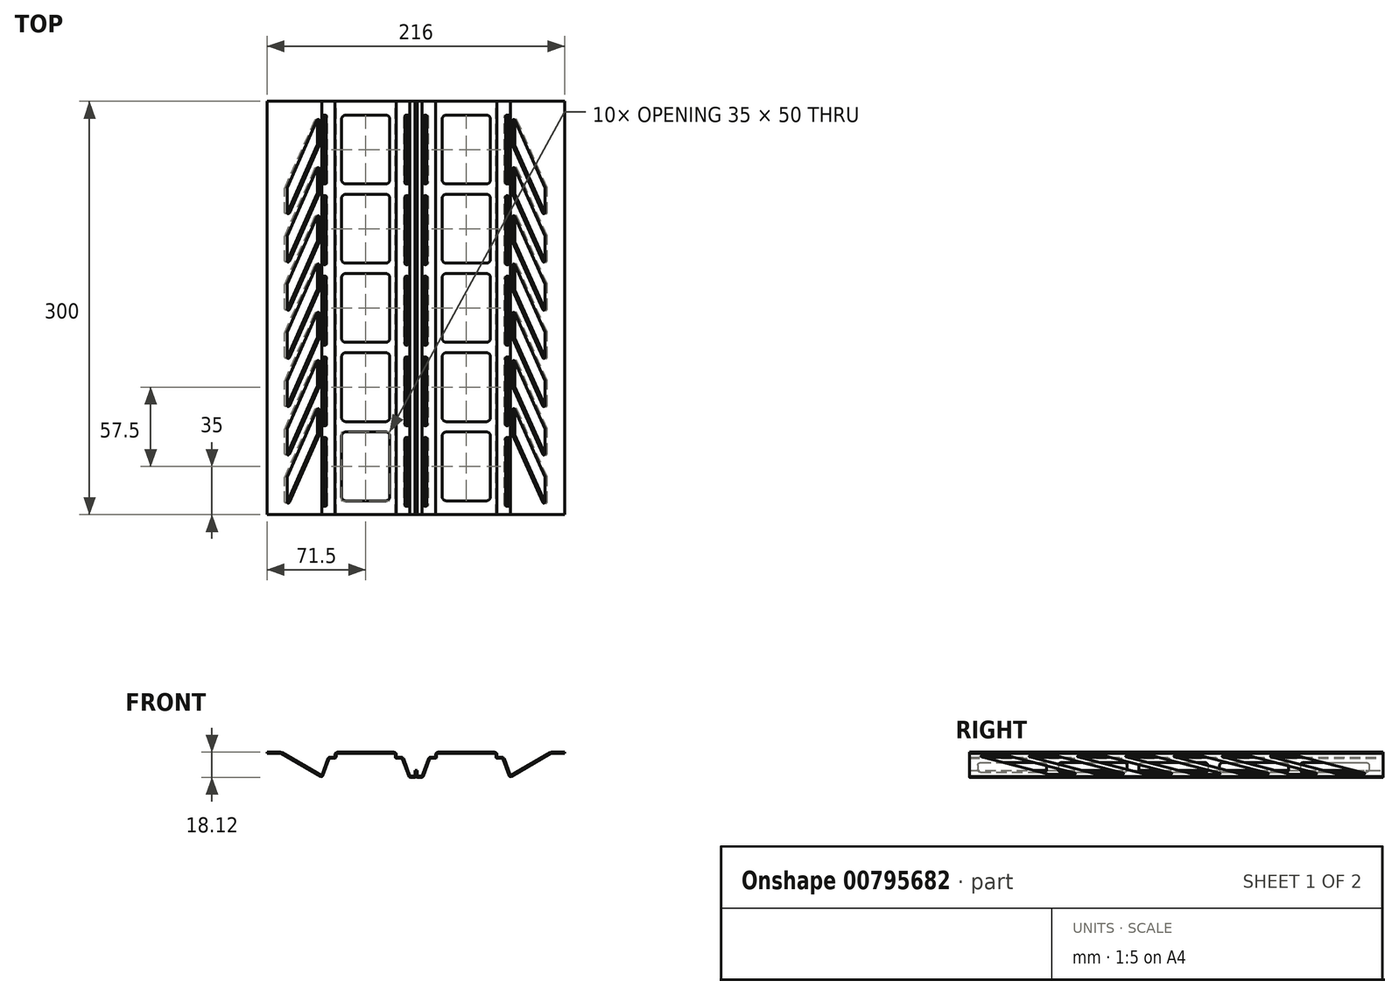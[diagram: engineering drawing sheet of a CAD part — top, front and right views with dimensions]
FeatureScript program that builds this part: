
annotation { "Feature Type Name" : "Feature", "Feature Type Description" : "" }
export const myFeature = defineFeature(function(context is Context, id is Id, definition is map)
    precondition{}
    {
        {
            var Q0;
            Q0=qCreatedBy(makeId("Front.planeOp"),FACE);
            var sketch = newSketch(context, id + "F0", { "sketchPlane" : qUnion([Q0])});
            skLineSegment(sketch, "E0", {"start": v(-0.8, 0) * mm, "end": v(-4.3, 0) * mm});
            skLineSegment(sketch, "E1", {"start": v(-5.24, 0.66) * mm, "end": v(-9.76, 13.08) * mm});
            skLineSegment(sketch, "E2", {"start": v(-10.7, 13.74) * mm, "end": v(-14, 13.74) * mm});
            skLineSegment(sketch, "E3", {"start": v(-63.24, 13.08) * mm, "end": v(-67.6, 1.12) * mm});
            skLineSegment(sketch, "E4", {"start": v(-69.03, 0.6) * mm, "end": v(-97.77, 17.19) * mm});
            skLineSegment(sketch, "E5", {"start": v(-98.27, 17.32) * mm, "end": v(-108, 17.32) * mm});
            skLineSegment(sketch, "E6", {"start": v(-57, 17.32) * mm, "end": v(-16, 17.32) * mm});
            skLineSegment(sketch, "E7", {"start": v(-58, 14.74) * mm, "end": v(-58, 16.32) * mm});
            skLineSegment(sketch, "E8", {"start": v(-36.5, 24.7) * mm, "end": v(-36.5, 3.7) * mm, "construction": true});
            skPoint(sketch, "E8.startSnap0", {"position": v(-36.5, 13.74) * mm});
            skLineSegment(sketch, "E9.MirrorCS", {"start": v(-15, 14.74) * mm, "end": v(-15, 16.32) * mm});
            skPoint(sketch, "E10.orphan", {"position": v(-63.46, 17.32) * mm});
            skLineSegment(sketch, "E11.trimOffspring", {"start": v(-59, 13.74) * mm, "end": v(-62.3, 13.74) * mm});
            skPoint(sketch, "E12.visualSharp", {"position": v(-15, 13.74) * mm});
            skArc(sketch, "E12.filletArc", {"start": v(-15, 14.74) * mm, "mid": v(-14.7, 14.03) * mm, "end": v(-14, 13.74) * mm});
            skPoint(sketch, "E13.visualSharp", {"position": v(-15, 17.32) * mm});
            skArc(sketch, "E13.filletArc", {"start": v(-15, 16.32) * mm, "mid": v(-15.3, 17.03) * mm, "end": v(-16, 17.32) * mm});
            skPoint(sketch, "E14.visualSharp", {"position": v(-58, 17.32) * mm});
            skArc(sketch, "E14.filletArc", {"start": v(-57, 17.32) * mm, "mid": v(-57.7, 17.03) * mm, "end": v(-58, 16.32) * mm});
            skPoint(sketch, "E15.visualSharp", {"position": v(-58, 13.74) * mm});
            skArc(sketch, "E15.filletArc", {"start": v(-59, 13.74) * mm, "mid": v(-58.3, 14.03) * mm, "end": v(-58, 14.74) * mm});
            skPoint(sketch, "E16.visualSharp", {"position": v(-63, 13.74) * mm});
            skArc(sketch, "E16.filletArc", {"start": v(-62.3, 13.74) * mm, "mid": v(-62.87, 13.56) * mm, "end": v(-63.24, 13.08) * mm});
            skPoint(sketch, "E17.visualSharp", {"position": v(-10, 13.74) * mm});
            skArc(sketch, "E17.filletArc", {"start": v(-9.76, 13.08) * mm, "mid": v(-10.13, 13.56) * mm, "end": v(-10.7, 13.74) * mm});
            skPoint(sketch, "E18.visualSharp", {"position": v(-5, 0) * mm});
            skArc(sketch, "E18.filletArc", {"start": v(-5.24, 0.66) * mm, "mid": v(-4.87, 0.18) * mm, "end": v(-4.3, 0) * mm});
            skPoint(sketch, "E19.visualSharp", {"position": v(-68, 0) * mm});
            skArc(sketch, "E19.filletArc", {"start": v(-69.03, 0.6) * mm, "mid": v(-68.2, 0.52) * mm, "end": v(-67.6, 1.12) * mm});
            skPoint(sketch, "E20.visualSharp", {"position": v(-98, 17.32) * mm});
            skArc(sketch, "E20.filletArc", {"start": v(-97.77, 17.19) * mm, "mid": v(-98, 17.29) * mm, "end": v(-98.27, 17.32) * mm});
            skLineSegment(sketch, "E21.0", {"start": v(-68.43, 1.17) * mm, "end": v(-97.37, 17.88) * mm});
            skLineSegment(sketch, "E21.1", {"start": v(-64, 13.35) * mm, "end": v(-68.43, 1.17) * mm});
            skArc(sketch, "E21.2", {"start": v(-62.3, 14.54) * mm, "mid": v(-63.33, 14.21) * mm, "end": v(-64, 13.35) * mm});
            skLineSegment(sketch, "E21.3", {"start": v(-10.7, 14.54) * mm, "end": v(-14.2, 14.54) * mm});
            skArc(sketch, "E21.4", {"start": v(-9, 13.35) * mm, "mid": v(-9.67, 14.21) * mm, "end": v(-10.7, 14.54) * mm});
            skLineSegment(sketch, "E21.5", {"start": v(-4.44, 0.8) * mm, "end": v(-9, 13.35) * mm});
            skLineSegment(sketch, "E21.6", {"start": v(-0.8, 0.8) * mm, "end": v(-4.44, 0.8) * mm});
            skLineSegment(sketch, "E21.7", {"start": v(-14.2, 14.54) * mm, "end": v(-14.2, 16.32) * mm});
            skArc(sketch, "E21.8", {"start": v(-14.2, 16.32) * mm, "mid": v(-14.73, 17.6) * mm, "end": v(-16, 18.12) * mm});
            skLineSegment(sketch, "E21.9", {"start": v(-57, 18.12) * mm, "end": v(-16, 18.12) * mm});
            skArc(sketch, "E21.10", {"start": v(-57, 18.12) * mm, "mid": v(-58.27, 17.6) * mm, "end": v(-58.8, 16.32) * mm});
            skLineSegment(sketch, "E21.11", {"start": v(-58.8, 14.54) * mm, "end": v(-58.8, 16.32) * mm});
            skLineSegment(sketch, "E21.12", {"start": v(-58.8, 14.54) * mm, "end": v(-62.3, 14.54) * mm});
            skLineSegment(sketch, "E22.0", {"start": v(-98.27, 18.12) * mm, "end": v(-108, 18.12) * mm});
            skArc(sketch, "E22.1", {"start": v(-97.37, 17.88) * mm, "mid": v(-97.8, 18.06) * mm, "end": v(-98.27, 18.12) * mm});
            skLineSegment(sketch, "E23", {"start": v(-108, 18.12) * mm, "end": v(-108, 17.32) * mm});
            skLineSegment(sketch, "E24.0", {"start": v(-0.8, 0.8) * mm, "end": v(-0.8, 4.9) * mm});
            skLineSegment(sketch, "E25", {"start": v(0, 4.9) * mm, "end": v(-0.8, 4.9) * mm});
            skLineSegment(sketch, "E26", {"start": v(0, 4.9) * mm, "end": v(0, 0.8) * mm});
            skPoint(sketch, "E27.visualSharp", {"position": v(0, 0) * mm});
            skArc(sketch, "E27.filletArc", {"start": v(-0.8, 0) * mm, "mid": v(-0.23, 0.23) * mm, "end": v(0, 0.8) * mm});
            skSolve(sketch);
        }
        {
            var Q0;
            Q0=makeQuery(id+"F0.imprint","IMPRINT",FACE,{"disambiguationData":[TD([[makeQuery(id+"F0.imprint","IMPRINT",EDGE,{"derivedFrom":sQuery(id+"F0.wireOp",EDGE,"E0")}),-1.0]])]});
            extrude(context, id + "F1", {"entities" : qUnion([Q0]), "depth" : 300 * mm, "offsetDistance" : 25 * mm});
        }
        {
            var Q0;
            Q0=makeQuery(id+"F1.opExtrude","SWEPT_FACE",FACE,{"disambiguationData":[OSD([sQuery(id+"F0.wireOp",EDGE,"E21.9")])]});
            var sketch = newSketch(context, id + "F2", { "sketchPlane" : qUnion([Q0])});
            skLineSegment(sketch, "E28", {"start": v(-36.5, 0) * mm, "end": v(-36.5, -305.2) * mm, "construction": true});
            skPoint(sketch, "E29", {"position": v(-36.5, -35) * mm});
            skLineSegment(sketch, "E30.bottom", {"start": v(-22, -60) * mm, "end": v(-51, -60) * mm});
            skLineSegment(sketch, "E30.top", {"start": v(-22, -10) * mm, "end": v(-51, -10) * mm});
            skLineSegment(sketch, "E30.left", {"start": v(-19, -57) * mm, "end": v(-19, -13) * mm});
            skLineSegment(sketch, "E30.right", {"start": v(-54, -57) * mm, "end": v(-54, -13) * mm});
            skPoint(sketch, "E31.visualSharp", {"position": v(-54, -10) * mm});
            skArc(sketch, "E31.filletArc", {"start": v(-51, -10) * mm, "mid": v(-53.12, -10.88) * mm, "end": v(-54, -13) * mm});
            skPoint(sketch, "E32.visualSharp", {"position": v(-19, -10) * mm});
            skArc(sketch, "E32.filletArc", {"start": v(-19, -13) * mm, "mid": v(-19.88, -10.88) * mm, "end": v(-22, -10) * mm});
            skPoint(sketch, "E33.visualSharp", {"position": v(-19, -60) * mm});
            skArc(sketch, "E33.filletArc", {"start": v(-22, -60) * mm, "mid": v(-19.88, -59.12) * mm, "end": v(-19, -57) * mm});
            skPoint(sketch, "E34.visualSharp", {"position": v(-54, -60) * mm});
            skArc(sketch, "E34.filletArc", {"start": v(-54, -57) * mm, "mid": v(-53.12, -59.12) * mm, "end": v(-51, -60) * mm});
            skLineSegment(sketch, "E35.0.1.0", {"start": v(-22, -67.5) * mm, "end": v(-51, -67.5) * mm});
            skArc(sketch, "E35.0.1.1", {"start": v(-51, -67.5) * mm, "mid": v(-53.12, -68.38) * mm, "end": v(-54, -70.5) * mm});
            skLineSegment(sketch, "E35.0.1.2", {"start": v(-54, -114.5) * mm, "end": v(-54, -70.5) * mm});
            skArc(sketch, "E35.0.1.3", {"start": v(-54, -114.5) * mm, "mid": v(-53.12, -116.62) * mm, "end": v(-51, -117.5) * mm});
            skLineSegment(sketch, "E35.0.1.4", {"start": v(-22, -117.5) * mm, "end": v(-51, -117.5) * mm});
            skArc(sketch, "E35.0.1.5", {"start": v(-22, -117.5) * mm, "mid": v(-19.88, -116.62) * mm, "end": v(-19, -114.5) * mm});
            skLineSegment(sketch, "E35.0.1.6", {"start": v(-19, -114.5) * mm, "end": v(-19, -70.5) * mm});
            skArc(sketch, "E35.0.1.7", {"start": v(-19, -70.5) * mm, "mid": v(-19.88, -68.38) * mm, "end": v(-22, -67.5) * mm});
            skLineSegment(sketch, "E35.0.2.0", {"start": v(-22, -125) * mm, "end": v(-51, -125) * mm});
            skArc(sketch, "E35.0.2.1", {"start": v(-51, -125) * mm, "mid": v(-53.12, -125.88) * mm, "end": v(-54, -128) * mm});
            skLineSegment(sketch, "E35.0.2.2", {"start": v(-54, -172) * mm, "end": v(-54, -128) * mm});
            skArc(sketch, "E35.0.2.3", {"start": v(-54, -172) * mm, "mid": v(-53.12, -174.12) * mm, "end": v(-51, -175) * mm});
            skLineSegment(sketch, "E35.0.2.4", {"start": v(-22, -175) * mm, "end": v(-51, -175) * mm});
            skArc(sketch, "E35.0.2.5", {"start": v(-22, -175) * mm, "mid": v(-19.88, -174.12) * mm, "end": v(-19, -172) * mm});
            skLineSegment(sketch, "E35.0.2.6", {"start": v(-19, -172) * mm, "end": v(-19, -128) * mm});
            skArc(sketch, "E35.0.2.7", {"start": v(-19, -128) * mm, "mid": v(-19.88, -125.88) * mm, "end": v(-22, -125) * mm});
            skLineSegment(sketch, "E35.0.3.0", {"start": v(-22, -182.5) * mm, "end": v(-51, -182.5) * mm});
            skArc(sketch, "E35.0.3.1", {"start": v(-51, -182.5) * mm, "mid": v(-53.12, -183.38) * mm, "end": v(-54, -185.5) * mm});
            skLineSegment(sketch, "E35.0.3.2", {"start": v(-54, -229.5) * mm, "end": v(-54, -185.5) * mm});
            skArc(sketch, "E35.0.3.3", {"start": v(-54, -229.5) * mm, "mid": v(-53.12, -231.62) * mm, "end": v(-51, -232.5) * mm});
            skLineSegment(sketch, "E35.0.3.4", {"start": v(-22, -232.5) * mm, "end": v(-51, -232.5) * mm});
            skArc(sketch, "E35.0.3.5", {"start": v(-22, -232.5) * mm, "mid": v(-19.88, -231.62) * mm, "end": v(-19, -229.5) * mm});
            skLineSegment(sketch, "E35.0.3.6", {"start": v(-19, -229.5) * mm, "end": v(-19, -185.5) * mm});
            skArc(sketch, "E35.0.3.7", {"start": v(-19, -185.5) * mm, "mid": v(-19.88, -183.38) * mm, "end": v(-22, -182.5) * mm});
            skLineSegment(sketch, "E35.0.4.0", {"start": v(-22, -240) * mm, "end": v(-51, -240) * mm});
            skArc(sketch, "E35.0.4.1", {"start": v(-51, -240) * mm, "mid": v(-53.12, -240.88) * mm, "end": v(-54, -243) * mm});
            skLineSegment(sketch, "E35.0.4.2", {"start": v(-54, -287) * mm, "end": v(-54, -243) * mm});
            skArc(sketch, "E35.0.4.3", {"start": v(-54, -287) * mm, "mid": v(-53.12, -289.12) * mm, "end": v(-51, -290) * mm});
            skLineSegment(sketch, "E35.0.4.4", {"start": v(-22, -290) * mm, "end": v(-51, -290) * mm});
            skArc(sketch, "E35.0.4.5", {"start": v(-22, -290) * mm, "mid": v(-19.88, -289.12) * mm, "end": v(-19, -287) * mm});
            skLineSegment(sketch, "E35.0.4.6", {"start": v(-19, -287) * mm, "end": v(-19, -243) * mm});
            skArc(sketch, "E35.0.4.7", {"start": v(-19, -243) * mm, "mid": v(-19.88, -240.88) * mm, "end": v(-22, -240) * mm});
            skLineSegment(sketch, "E35.direction1", {"start": v(-51, -10) * mm, "end": v(-26, -10) * mm, "construction": true});
            skLineSegment(sketch, "E35.direction2", {"start": v(-51, -10) * mm, "end": v(-51, -67.5) * mm, "construction": true});
            skSolve(sketch);
        }
        {
            var Q0;
            Q0 = qSketchRegion(id + "F2", true);
            extrude(context, id + "F3", {"entities" : qUnion([Q0]), "operationType" : NewBodyOperationType.REMOVE, "oppositeDirection" : true, "depth" : 25 * mm, "offsetDistance" : 25 * mm});
        }
        {
            var Q0;
            Q0=makeQuery(id+"F1.opExtrude","SWEPT_FACE",FACE,{"disambiguationData":[OSD([sQuery(id+"F0.wireOp",EDGE,"E21.5")])]});
            var sketch = newSketch(context, id + "F4", { "sketchPlane" : qUnion([Q0])});
            skLineSegment(sketch, "E36", {"start": v(0, 8.95) * mm, "end": v(-300, 8.95) * mm, "construction": true});
            skPoint(sketch, "E37", {"position": v(-10, 8.95) * mm});
            skLineSegment(sketch, "E38.bottom", {"start": v(-12, 5.27) * mm, "end": v(-58, 5.27) * mm});
            skLineSegment(sketch, "E38.top", {"start": v(-12, 12.63) * mm, "end": v(-58, 12.63) * mm});
            skLineSegment(sketch, "E38.left", {"start": v(-10, 7.27) * mm, "end": v(-10, 10.63) * mm});
            skLineSegment(sketch, "E38.right", {"start": v(-60, 7.27) * mm, "end": v(-60, 10.63) * mm});
            skPoint(sketch, "E39.visualSharp", {"position": v(-10, 5.27) * mm});
            skArc(sketch, "E39.filletArc", {"start": v(-12, 5.27) * mm, "mid": v(-10.59, 5.86) * mm, "end": v(-10, 7.27) * mm});
            skPoint(sketch, "E40.visualSharp", {"position": v(-10, 12.63) * mm});
            skArc(sketch, "E40.filletArc", {"start": v(-10, 10.63) * mm, "mid": v(-10.59, 12.04) * mm, "end": v(-12, 12.63) * mm});
            skPoint(sketch, "E41.visualSharp", {"position": v(-60, 5.27) * mm});
            skArc(sketch, "E41.filletArc", {"start": v(-60, 7.27) * mm, "mid": v(-59.41, 5.86) * mm, "end": v(-58, 5.27) * mm});
            skPoint(sketch, "E42.visualSharp", {"position": v(-60, 12.63) * mm});
            skArc(sketch, "E42.filletArc", {"start": v(-58, 12.63) * mm, "mid": v(-59.41, 12.04) * mm, "end": v(-60, 10.63) * mm});
            skLineSegment(sketch, "E43.1.0.0", {"start": v(-67.5, 7.27) * mm, "end": v(-67.5, 10.63) * mm});
            skArc(sketch, "E43.1.0.1", {"start": v(-69.5, 5.27) * mm, "mid": v(-68.09, 5.86) * mm, "end": v(-67.5, 7.27) * mm});
            skArc(sketch, "E43.1.0.2", {"start": v(-67.5, 10.63) * mm, "mid": v(-68.09, 12.04) * mm, "end": v(-69.5, 12.63) * mm});
            skLineSegment(sketch, "E43.1.0.3", {"start": v(-69.5, 12.63) * mm, "end": v(-115.5, 12.63) * mm});
            skLineSegment(sketch, "E43.1.0.4", {"start": v(-69.5, 5.27) * mm, "end": v(-115.5, 5.27) * mm});
            skArc(sketch, "E43.1.0.5", {"start": v(-117.5, 7.27) * mm, "mid": v(-116.91, 5.86) * mm, "end": v(-115.5, 5.27) * mm});
            skLineSegment(sketch, "E43.1.0.6", {"start": v(-117.5, 7.27) * mm, "end": v(-117.5, 10.63) * mm});
            skArc(sketch, "E43.1.0.7", {"start": v(-115.5, 12.63) * mm, "mid": v(-116.91, 12.04) * mm, "end": v(-117.5, 10.63) * mm});
            skLineSegment(sketch, "E43.2.0.0", {"start": v(-125, 7.27) * mm, "end": v(-125, 10.63) * mm});
            skArc(sketch, "E43.2.0.1", {"start": v(-127, 5.27) * mm, "mid": v(-125.59, 5.86) * mm, "end": v(-125, 7.27) * mm});
            skArc(sketch, "E43.2.0.2", {"start": v(-125, 10.63) * mm, "mid": v(-125.59, 12.04) * mm, "end": v(-127, 12.63) * mm});
            skLineSegment(sketch, "E43.2.0.3", {"start": v(-127, 12.63) * mm, "end": v(-173, 12.63) * mm});
            skLineSegment(sketch, "E43.2.0.4", {"start": v(-127, 5.27) * mm, "end": v(-173, 5.27) * mm});
            skArc(sketch, "E43.2.0.5", {"start": v(-175, 7.27) * mm, "mid": v(-174.41, 5.86) * mm, "end": v(-173, 5.27) * mm});
            skLineSegment(sketch, "E43.2.0.6", {"start": v(-175, 7.27) * mm, "end": v(-175, 10.63) * mm});
            skArc(sketch, "E43.2.0.7", {"start": v(-173, 12.63) * mm, "mid": v(-174.41, 12.04) * mm, "end": v(-175, 10.63) * mm});
            skLineSegment(sketch, "E43.3.0.0", {"start": v(-182.5, 7.27) * mm, "end": v(-182.5, 10.63) * mm});
            skArc(sketch, "E43.3.0.1", {"start": v(-184.5, 5.27) * mm, "mid": v(-183.09, 5.86) * mm, "end": v(-182.5, 7.27) * mm});
            skArc(sketch, "E43.3.0.2", {"start": v(-182.5, 10.63) * mm, "mid": v(-183.09, 12.04) * mm, "end": v(-184.5, 12.63) * mm});
            skLineSegment(sketch, "E43.3.0.3", {"start": v(-184.5, 12.63) * mm, "end": v(-230.5, 12.63) * mm});
            skLineSegment(sketch, "E43.3.0.4", {"start": v(-184.5, 5.27) * mm, "end": v(-230.5, 5.27) * mm});
            skArc(sketch, "E43.3.0.5", {"start": v(-232.5, 7.27) * mm, "mid": v(-231.91, 5.86) * mm, "end": v(-230.5, 5.27) * mm});
            skLineSegment(sketch, "E43.3.0.6", {"start": v(-232.5, 7.27) * mm, "end": v(-232.5, 10.63) * mm});
            skArc(sketch, "E43.3.0.7", {"start": v(-230.5, 12.63) * mm, "mid": v(-231.91, 12.04) * mm, "end": v(-232.5, 10.63) * mm});
            skLineSegment(sketch, "E43.4.0.0", {"start": v(-240, 7.27) * mm, "end": v(-240, 10.63) * mm});
            skArc(sketch, "E43.4.0.1", {"start": v(-242, 5.27) * mm, "mid": v(-240.59, 5.86) * mm, "end": v(-240, 7.27) * mm});
            skArc(sketch, "E43.4.0.2", {"start": v(-240, 10.63) * mm, "mid": v(-240.59, 12.04) * mm, "end": v(-242, 12.63) * mm});
            skLineSegment(sketch, "E43.4.0.3", {"start": v(-242, 12.63) * mm, "end": v(-288, 12.63) * mm});
            skLineSegment(sketch, "E43.4.0.4", {"start": v(-242, 5.27) * mm, "end": v(-288, 5.27) * mm});
            skArc(sketch, "E43.4.0.5", {"start": v(-290, 7.27) * mm, "mid": v(-289.41, 5.86) * mm, "end": v(-288, 5.27) * mm});
            skLineSegment(sketch, "E43.4.0.6", {"start": v(-290, 7.27) * mm, "end": v(-290, 10.63) * mm});
            skArc(sketch, "E43.4.0.7", {"start": v(-288, 12.63) * mm, "mid": v(-289.41, 12.04) * mm, "end": v(-290, 10.63) * mm});
            skLineSegment(sketch, "E43.direction1", {"start": v(-10, 7.27) * mm, "end": v(-67.5, 7.27) * mm, "construction": true});
            skSolve(sketch);
        }
        {
            var Q0;
            Q0=qCreatedBy(makeId("Right.planeOp"),FACE);
            cPlane(context, id + "F5", {"entities" : qUnion([Q0]), "cplaneType" : CPlaneType.OFFSET, "offset" : 36.5 * mm, "oppositeDirection" : true, "width" : 150 * mm, "height" : 150 * mm});
        }
        {
            var Q0;
            Q0=qCreatedBy(id+"F5.planeOp",FACE);
            var sketch = newSketch(context, id + "F6", { "sketchPlane" : qUnion([Q0])});
            skLineSegment(sketch, "E44.0", {"start": v(-60, 5.5) * mm, "end": v(-60, 8.65) * mm});
            skEllipticalArc(sketch, "E45.0", {});
            skLineSegment(sketch, "E46.0", {"start": v(-12, 3.62) * mm, "end": v(-58, 3.62) * mm});
            skLineSegment(sketch, "E47.0", {"start": v(-12, 10.53) * mm, "end": v(-58, 10.53) * mm});
            skPoint(sketch, "E48.0", {"position": v(-59.41, 9.98) * mm});
            skEllipticalArc(sketch, "E49.0", {});
            skEllipticalArc(sketch, "E50.0", {});
            skLineSegment(sketch, "E51.0", {"start": v(-10, 5.5) * mm, "end": v(-10, 8.65) * mm});
            skEllipticalArc(sketch, "E52.0", {});
            skPoint(sketch, "E53.0.end.orphan", {"position": v(-115.5, 3.62) * mm});
            skPoint(sketch, "E53.0.start.orphan", {"position": v(-69.5, 3.62) * mm});
            skPoint(sketch, "E54.0.end.orphan", {"position": v(-67.5, 5.5) * mm});
            skPoint(sketch, "E55.0.end.orphan", {"position": v(-67.5, 8.65) * mm});
            skLineSegment(sketch, "E56.1.0.0", {"start": v(-70.5, 3.62) * mm, "end": v(-116.5, 3.62) * mm});
            skEllipticalArc(sketch, "E56.1.0.1", {});
            skLineSegment(sketch, "E56.1.0.2", {"start": v(-118.5, 5.5) * mm, "end": v(-118.5, 8.65) * mm});
            skEllipticalArc(sketch, "E56.1.0.3", {});
            skLineSegment(sketch, "E56.1.0.4", {"start": v(-70.5, 10.53) * mm, "end": v(-116.5, 10.53) * mm});
            skEllipticalArc(sketch, "E56.1.0.5", {});
            skLineSegment(sketch, "E56.1.0.6", {"start": v(-68.5, 5.5) * mm, "end": v(-68.5, 8.65) * mm});
            skEllipticalArc(sketch, "E56.1.0.7", {});
            skLineSegment(sketch, "E56.2.0.0", {"start": v(-129, 3.62) * mm, "end": v(-175, 3.62) * mm});
            skEllipticalArc(sketch, "E56.2.0.1", {});
            skLineSegment(sketch, "E56.2.0.2", {"start": v(-177, 5.5) * mm, "end": v(-177, 8.65) * mm});
            skEllipticalArc(sketch, "E56.2.0.3", {});
            skLineSegment(sketch, "E56.2.0.4", {"start": v(-129, 10.53) * mm, "end": v(-175, 10.53) * mm});
            skEllipticalArc(sketch, "E56.2.0.5", {});
            skLineSegment(sketch, "E56.2.0.6", {"start": v(-127, 5.5) * mm, "end": v(-127, 8.65) * mm});
            skEllipticalArc(sketch, "E56.2.0.7", {});
            skLineSegment(sketch, "E56.3.0.0", {"start": v(-187.5, 3.62) * mm, "end": v(-233.5, 3.62) * mm});
            skEllipticalArc(sketch, "E56.3.0.1", {});
            skLineSegment(sketch, "E56.3.0.2", {"start": v(-235.5, 5.5) * mm, "end": v(-235.5, 8.65) * mm});
            skEllipticalArc(sketch, "E56.3.0.3", {});
            skLineSegment(sketch, "E56.3.0.4", {"start": v(-187.5, 10.53) * mm, "end": v(-233.5, 10.53) * mm});
            skEllipticalArc(sketch, "E56.3.0.5", {});
            skLineSegment(sketch, "E56.3.0.6", {"start": v(-185.5, 5.5) * mm, "end": v(-185.5, 8.65) * mm});
            skEllipticalArc(sketch, "E56.3.0.7", {});
            skLineSegment(sketch, "E56.4.0.0", {"start": v(-246, 3.62) * mm, "end": v(-292, 3.62) * mm});
            skEllipticalArc(sketch, "E56.4.0.1", {});
            skLineSegment(sketch, "E56.4.0.2", {"start": v(-294, 5.5) * mm, "end": v(-294, 8.65) * mm});
            skEllipticalArc(sketch, "E56.4.0.3", {});
            skLineSegment(sketch, "E56.4.0.4", {"start": v(-246, 10.53) * mm, "end": v(-292, 10.53) * mm});
            skEllipticalArc(sketch, "E56.4.0.5", {});
            skLineSegment(sketch, "E56.4.0.6", {"start": v(-244, 5.5) * mm, "end": v(-244, 8.65) * mm});
            skEllipticalArc(sketch, "E56.4.0.7", {});
            skLineSegment(sketch, "E56.direction1", {"start": v(-58, 3.62) * mm, "end": v(-116.5, 3.62) * mm, "construction": true});
            const initialGuessF6  = {"E45.0": [-0.058, 0.005498463103929539, 1, 0, 0.002, 0.001879385241571812, 3.141592653589793, 4.71238898038469], "E49.0": [-0.058, 0.008654560251329744, 1, 0, 0.002, 0.001879385241571817, 1.5707963267948966, 3.141592653589793], "E50.0": [-0.012, 0.005498463103929544, 1, 0, 0.002, 0.001879385241571817, 4.71238898038469, 0], "E52.0": [-0.012, 0.00865456025132975, 1, 0, 0.002, 0.001879385241571817, 0, 1.5707963267948966], "E56.1.0.1": [-0.1165, 0.005498463103929539, 1, 0, 0.002, 0.001879385241571812, 3.141592653589793, 4.71238898038469], "E56.1.0.3": [-0.1165, 0.008654560251329744, 1, 0, 0.002, 0.001879385241571817, 1.5707963267948966, 3.141592653589793], "E56.1.0.5": [-0.0705, 0.00865456025132975, 1, 0, 0.002, 0.001879385241571817, 0, 1.5707963267948966], "E56.1.0.7": [-0.0705, 0.005498463103929544, 1, 0, 0.002, 0.001879385241571817, 4.71238898038469, 0], "E56.2.0.1": [-0.175, 0.005498463103929539, 1, 0, 0.002, 0.001879385241571812, 3.141592653589793, 4.71238898038469], "E56.2.0.3": [-0.175, 0.008654560251329744, 1, 0, 0.002, 0.001879385241571817, 1.5707963267948966, 3.141592653589793], "E56.2.0.5": [-0.129, 0.00865456025132975, 1, 0, 0.002, 0.001879385241571817, 0, 1.5707963267948966], "E56.2.0.7": [-0.129, 0.005498463103929544, 1, 0, 0.002, 0.001879385241571817, 4.71238898038469, 0], "E56.3.0.1": [-0.2335, 0.005498463103929539, 1, 0, 0.002, 0.001879385241571812, 3.141592653589793, 4.71238898038469], "E56.3.0.3": [-0.2335, 0.008654560251329744, 1, 0, 0.002, 0.001879385241571817, 1.5707963267948966, 3.141592653589793], "E56.3.0.5": [-0.1875, 0.00865456025132975, 1, 0, 0.002, 0.001879385241571817, 0, 1.5707963267948966], "E56.3.0.7": [-0.1875, 0.005498463103929544, 1, 0, 0.002, 0.001879385241571817, 4.71238898038469, 0], "E56.4.0.1": [-0.292, 0.005498463103929539, 1, 0, 0.002, 0.001879385241571812, 3.141592653589793, 4.71238898038469], "E56.4.0.3": [-0.292, 0.008654560251329744, 1, 0, 0.002, 0.001879385241571817, 1.5707963267948966, 3.141592653589793], "E56.4.0.5": [-0.246, 0.00865456025132975, 1, 0, 0.002, 0.001879385241571817, 0, 1.5707963267948966], "E56.4.0.7": [-0.246, 0.005498463103929544, 1, 0, 0.002, 0.001879385241571817, 4.71238898038469, 0]};
            skSetInitialGuess(sketch, initialGuessF6);
            skSolve(sketch);
        }
        {
            var Q0;
            Q0 = qSketchRegion(id + "F6", true);
            extrude(context, id + "F7", {"entities" : qUnion([Q0]), "operationType" : NewBodyOperationType.REMOVE, "endBound" : BoundingType.SYMMETRIC, "depth" : 70 * mm, "offsetDistance" : 25 * mm});
        }
        {
            var Q0;
            Q0=makeQuery(id+"F1.opExtrude","SWEPT_BODY",BODY,{"disambiguationData":[OSD([sQuery(id+"F0.wireOp",EDGE,"E0"),sQuery(id+"F0.wireOp",EDGE,"E1"),sQuery(id+"F0.wireOp",EDGE,"E2"),sQuery(id+"F0.wireOp",EDGE,"E3"),sQuery(id+"F0.wireOp",EDGE,"E4"),sQuery(id+"F0.wireOp",EDGE,"E5"),sQuery(id+"F0.wireOp",EDGE,"E6"),sQuery(id+"F0.wireOp",EDGE,"E7"),sQuery(id+"F0.wireOp",EDGE,"E9.MirrorCS"),sQuery(id+"F0.wireOp",EDGE,"E11.trimOffspring"),sQuery(id+"F0.wireOp",EDGE,"E12.filletArc"),sQuery(id+"F0.wireOp",EDGE,"E13.filletArc"),sQuery(id+"F0.wireOp",EDGE,"E14.filletArc"),sQuery(id+"F0.wireOp",EDGE,"E15.filletArc"),sQuery(id+"F0.wireOp",EDGE,"E16.filletArc"),sQuery(id+"F0.wireOp",EDGE,"E17.filletArc"),sQuery(id+"F0.wireOp",EDGE,"E18.filletArc"),sQuery(id+"F0.wireOp",EDGE,"E19.filletArc"),sQuery(id+"F0.wireOp",EDGE,"E20.filletArc"),sQuery(id+"F0.wireOp",EDGE,"E21.0"),sQuery(id+"F0.wireOp",EDGE,"E21.1"),sQuery(id+"F0.wireOp",EDGE,"E21.2"),sQuery(id+"F0.wireOp",EDGE,"E21.3"),sQuery(id+"F0.wireOp",EDGE,"E21.4"),sQuery(id+"F0.wireOp",EDGE,"E21.5"),sQuery(id+"F0.wireOp",EDGE,"E21.6"),sQuery(id+"F0.wireOp",EDGE,"E21.7"),sQuery(id+"F0.wireOp",EDGE,"E21.8"),sQuery(id+"F0.wireOp",EDGE,"E21.9"),sQuery(id+"F0.wireOp",EDGE,"E21.10"),sQuery(id+"F0.wireOp",EDGE,"E21.11"),sQuery(id+"F0.wireOp",EDGE,"E21.12"),sQuery(id+"F0.wireOp",EDGE,"E22.0"),sQuery(id+"F0.wireOp",EDGE,"E22.1"),sQuery(id+"F0.wireOp",EDGE,"E23"),sQuery(id+"F0.wireOp",EDGE,"E24.0"),sQuery(id+"F0.wireOp",EDGE,"E25"),sQuery(id+"F0.wireOp",EDGE,"E26"),sQuery(id+"F0.wireOp",EDGE,"E27.filletArc")])]});
            var Q1;
            Q1=qCreatedBy(makeId("Right.planeOp"),FACE);
            mirror(context, id + "F8", {"operationType" : NewBodyOperationType.ADD, "entities" : qUnion([Q0]), "mirrorPlane" : qUnion([Q1])});
        }
        {
            var Q0;
            Q0=makeQuery(id+"F8.opPattern","COPY",FACE,{"derivedFrom":makeQuery(id+"F1.opExtrude","SWEPT_FACE",FACE,{"disambiguationData":[OSD([sQuery(id+"F0.wireOp",EDGE,"E4")])]}),"instanceName":"1"});
            var sketch = newSketch(context, id + "F9", { "sketchPlane" : qUnion([Q0])});
            skLineSegment(sketch, "E57", {"start": v(63.08, 14.14) * mm, "end": v(63.08, 31.64) * mm});
            skLineSegment(sketch, "E58", {"start": v(63.2, 32.1) * mm, "end": v(88.37, 81.12) * mm});
            skLineSegment(sketch, "E59", {"start": v(90.26, 80.66) * mm, "end": v(90.26, 63.15) * mm});
            skLineSegment(sketch, "E60", {"start": v(90.15, 62.7) * mm, "end": v(64.97, 13.68) * mm});
            skPoint(sketch, "E61.visualSharp", {"position": v(63.08, 10) * mm});
            skArc(sketch, "E61.filletArc", {"start": v(63.08, 14.14) * mm, "mid": v(63.85, 13.16) * mm, "end": v(64.97, 13.68) * mm});
            skPoint(sketch, "E62.visualSharp", {"position": v(63.08, 31.88) * mm});
            skArc(sketch, "E62.filletArc", {"start": v(63.2, 32.1) * mm, "mid": v(63.1, 31.88) * mm, "end": v(63.08, 31.64) * mm});
            skPoint(sketch, "E63.visualSharp", {"position": v(90.26, 84.8) * mm});
            skArc(sketch, "E63.filletArc", {"start": v(90.26, 80.66) * mm, "mid": v(89.5, 81.63) * mm, "end": v(88.37, 81.12) * mm});
            skPoint(sketch, "E64.visualSharp", {"position": v(90.26, 62.91) * mm});
            skArc(sketch, "E64.filletArc", {"start": v(90.15, 62.7) * mm, "mid": v(90.23, 62.92) * mm, "end": v(90.26, 63.15) * mm});
            skLineSegment(sketch, "E65.0.1.0", {"start": v(90.15, 97.7) * mm, "end": v(64.97, 48.68) * mm});
            skLineSegment(sketch, "E65.0.1.1", {"start": v(63.08, 49.14) * mm, "end": v(63.08, 66.64) * mm});
            skArc(sketch, "E65.0.1.2", {"start": v(63.2, 67.1) * mm, "mid": v(63.1, 66.88) * mm, "end": v(63.08, 66.64) * mm});
            skLineSegment(sketch, "E65.0.1.3", {"start": v(63.2, 67.1) * mm, "end": v(88.37, 116.12) * mm});
            skArc(sketch, "E65.0.1.4", {"start": v(63.08, 49.14) * mm, "mid": v(63.85, 48.16) * mm, "end": v(64.97, 48.68) * mm});
            skLineSegment(sketch, "E65.0.1.5", {"start": v(90.26, 115.66) * mm, "end": v(90.26, 98.15) * mm});
            skArc(sketch, "E65.0.1.6", {"start": v(90.26, 115.66) * mm, "mid": v(89.5, 116.63) * mm, "end": v(88.37, 116.12) * mm});
            skArc(sketch, "E65.0.1.7", {"start": v(90.15, 97.7) * mm, "mid": v(90.23, 97.92) * mm, "end": v(90.26, 98.15) * mm});
            skLineSegment(sketch, "E65.0.2.0", {"start": v(90.15, 132.7) * mm, "end": v(64.97, 83.68) * mm});
            skLineSegment(sketch, "E65.0.2.1", {"start": v(63.08, 84.14) * mm, "end": v(63.08, 101.64) * mm});
            skArc(sketch, "E65.0.2.2", {"start": v(63.2, 102.1) * mm, "mid": v(63.1, 101.88) * mm, "end": v(63.08, 101.64) * mm});
            skLineSegment(sketch, "E65.0.2.3", {"start": v(63.2, 102.1) * mm, "end": v(88.37, 151.12) * mm});
            skArc(sketch, "E65.0.2.4", {"start": v(63.08, 84.14) * mm, "mid": v(63.85, 83.16) * mm, "end": v(64.97, 83.68) * mm});
            skLineSegment(sketch, "E65.0.2.5", {"start": v(90.26, 150.66) * mm, "end": v(90.26, 133.15) * mm});
            skArc(sketch, "E65.0.2.6", {"start": v(90.26, 150.66) * mm, "mid": v(89.5, 151.63) * mm, "end": v(88.37, 151.12) * mm});
            skArc(sketch, "E65.0.2.7", {"start": v(90.15, 132.7) * mm, "mid": v(90.23, 132.92) * mm, "end": v(90.26, 133.15) * mm});
            skLineSegment(sketch, "E65.0.3.0", {"start": v(90.15, 167.7) * mm, "end": v(64.97, 118.68) * mm});
            skLineSegment(sketch, "E65.0.3.1", {"start": v(63.08, 119.14) * mm, "end": v(63.08, 136.64) * mm});
            skArc(sketch, "E65.0.3.2", {"start": v(63.2, 137.1) * mm, "mid": v(63.1, 136.88) * mm, "end": v(63.08, 136.64) * mm});
            skLineSegment(sketch, "E65.0.3.3", {"start": v(63.2, 137.1) * mm, "end": v(88.37, 186.12) * mm});
            skArc(sketch, "E65.0.3.4", {"start": v(63.08, 119.14) * mm, "mid": v(63.85, 118.16) * mm, "end": v(64.97, 118.68) * mm});
            skLineSegment(sketch, "E65.0.3.5", {"start": v(90.26, 185.66) * mm, "end": v(90.26, 168.15) * mm});
            skArc(sketch, "E65.0.3.6", {"start": v(90.26, 185.66) * mm, "mid": v(89.5, 186.63) * mm, "end": v(88.37, 186.12) * mm});
            skArc(sketch, "E65.0.3.7", {"start": v(90.15, 167.7) * mm, "mid": v(90.23, 167.92) * mm, "end": v(90.26, 168.15) * mm});
            skLineSegment(sketch, "E65.0.4.0", {"start": v(90.15, 202.7) * mm, "end": v(64.97, 153.68) * mm});
            skLineSegment(sketch, "E65.0.4.1", {"start": v(63.08, 154.14) * mm, "end": v(63.08, 171.64) * mm});
            skArc(sketch, "E65.0.4.2", {"start": v(63.2, 172.1) * mm, "mid": v(63.1, 171.88) * mm, "end": v(63.08, 171.64) * mm});
            skLineSegment(sketch, "E65.0.4.3", {"start": v(63.2, 172.1) * mm, "end": v(88.37, 221.12) * mm});
            skArc(sketch, "E65.0.4.4", {"start": v(63.08, 154.14) * mm, "mid": v(63.85, 153.16) * mm, "end": v(64.97, 153.68) * mm});
            skLineSegment(sketch, "E65.0.4.5", {"start": v(90.26, 220.66) * mm, "end": v(90.26, 203.15) * mm});
            skArc(sketch, "E65.0.4.6", {"start": v(90.26, 220.66) * mm, "mid": v(89.5, 221.63) * mm, "end": v(88.37, 221.12) * mm});
            skArc(sketch, "E65.0.4.7", {"start": v(90.15, 202.7) * mm, "mid": v(90.23, 202.92) * mm, "end": v(90.26, 203.15) * mm});
            skLineSegment(sketch, "E65.0.5.0", {"start": v(90.15, 237.7) * mm, "end": v(64.97, 188.68) * mm});
            skLineSegment(sketch, "E65.0.5.1", {"start": v(63.08, 189.14) * mm, "end": v(63.08, 206.64) * mm});
            skArc(sketch, "E65.0.5.2", {"start": v(63.2, 207.1) * mm, "mid": v(63.1, 206.88) * mm, "end": v(63.08, 206.64) * mm});
            skLineSegment(sketch, "E65.0.5.3", {"start": v(63.2, 207.1) * mm, "end": v(88.37, 256.12) * mm});
            skArc(sketch, "E65.0.5.4", {"start": v(63.08, 189.14) * mm, "mid": v(63.85, 188.16) * mm, "end": v(64.97, 188.68) * mm});
            skLineSegment(sketch, "E65.0.5.5", {"start": v(90.26, 255.66) * mm, "end": v(90.26, 238.15) * mm});
            skArc(sketch, "E65.0.5.6", {"start": v(90.26, 255.66) * mm, "mid": v(89.5, 256.63) * mm, "end": v(88.37, 256.12) * mm});
            skArc(sketch, "E65.0.5.7", {"start": v(90.15, 237.7) * mm, "mid": v(90.23, 237.92) * mm, "end": v(90.26, 238.15) * mm});
            skLineSegment(sketch, "E65.0.6.0", {"start": v(90.15, 272.7) * mm, "end": v(64.97, 223.68) * mm});
            skLineSegment(sketch, "E65.0.6.1", {"start": v(63.08, 224.14) * mm, "end": v(63.08, 241.64) * mm});
            skArc(sketch, "E65.0.6.2", {"start": v(63.2, 242.1) * mm, "mid": v(63.1, 241.88) * mm, "end": v(63.08, 241.64) * mm});
            skLineSegment(sketch, "E65.0.6.3", {"start": v(63.2, 242.1) * mm, "end": v(88.37, 291.12) * mm});
            skArc(sketch, "E65.0.6.4", {"start": v(63.08, 224.14) * mm, "mid": v(63.85, 223.16) * mm, "end": v(64.97, 223.68) * mm});
            skLineSegment(sketch, "E65.0.6.5", {"start": v(90.26, 290.66) * mm, "end": v(90.26, 273.15) * mm});
            skArc(sketch, "E65.0.6.6", {"start": v(90.26, 290.66) * mm, "mid": v(89.5, 291.63) * mm, "end": v(88.37, 291.12) * mm});
            skArc(sketch, "E65.0.6.7", {"start": v(90.15, 272.7) * mm, "mid": v(90.23, 272.92) * mm, "end": v(90.26, 273.15) * mm});
            skLineSegment(sketch, "E65.direction1", {"start": v(64.97, 13.68) * mm, "end": v(89.97, 13.68) * mm, "construction": true});
            skLineSegment(sketch, "E65.direction2", {"start": v(64.97, 13.68) * mm, "end": v(64.97, 48.68) * mm, "construction": true});
            skSolve(sketch);
        }
        {
            var Q0;
            Q0=qCreatedBy(makeId("Right.planeOp"),FACE);
            var sketch = newSketch(context, id + "F10", { "sketchPlane" : qUnion([Q0])});
            skLineSegment(sketch, "E66.0.0", {"start": v(-273.15, 15.69) * mm, "end": v(-290.66, 15.69) * mm});
            skEllipticalArc(sketch, "E66.0.1", {});
            skLineSegment(sketch, "E66.0.2", {"start": v(-291.12, 14.74) * mm, "end": v(-242.1, 2.15) * mm});
            skEllipticalArc(sketch, "E66.0.3", {});
            skLineSegment(sketch, "E66.0.4", {"start": v(-241.64, 2.1) * mm, "end": v(-224.14, 2.1) * mm});
            skEllipticalArc(sketch, "E66.0.5", {});
            skLineSegment(sketch, "E66.0.6", {"start": v(-223.68, 3.04) * mm, "end": v(-272.7, 15.63) * mm});
            skEllipticalArc(sketch, "E66.0.7", {});
            skLineSegment(sketch, "E67.1.0.0", {"start": v(-238.15, 15.69) * mm, "end": v(-255.66, 15.69) * mm});
            skEllipticalArc(sketch, "E67.1.0.1", {});
            skLineSegment(sketch, "E67.1.0.2", {"start": v(-188.68, 3.04) * mm, "end": v(-237.7, 15.63) * mm});
            skLineSegment(sketch, "E67.1.0.3", {"start": v(-256.12, 14.74) * mm, "end": v(-207.1, 2.15) * mm});
            skEllipticalArc(sketch, "E67.1.0.4", {});
            skEllipticalArc(sketch, "E67.1.0.5", {});
            skLineSegment(sketch, "E67.1.0.6", {"start": v(-206.64, 2.1) * mm, "end": v(-189.14, 2.1) * mm});
            skEllipticalArc(sketch, "E67.1.0.7", {});
            skLineSegment(sketch, "E67.2.0.0", {"start": v(-203.15, 15.69) * mm, "end": v(-220.66, 15.69) * mm});
            skEllipticalArc(sketch, "E67.2.0.1", {});
            skLineSegment(sketch, "E67.2.0.2", {"start": v(-153.68, 3.04) * mm, "end": v(-202.7, 15.63) * mm});
            skLineSegment(sketch, "E67.2.0.3", {"start": v(-221.12, 14.74) * mm, "end": v(-172.1, 2.15) * mm});
            skEllipticalArc(sketch, "E67.2.0.4", {});
            skEllipticalArc(sketch, "E67.2.0.5", {});
            skLineSegment(sketch, "E67.2.0.6", {"start": v(-171.64, 2.1) * mm, "end": v(-154.14, 2.1) * mm});
            skEllipticalArc(sketch, "E67.2.0.7", {});
            skLineSegment(sketch, "E67.3.0.0", {"start": v(-168.15, 15.69) * mm, "end": v(-185.66, 15.69) * mm});
            skEllipticalArc(sketch, "E67.3.0.1", {});
            skLineSegment(sketch, "E67.3.0.2", {"start": v(-118.68, 3.04) * mm, "end": v(-167.7, 15.63) * mm});
            skLineSegment(sketch, "E67.3.0.3", {"start": v(-186.12, 14.74) * mm, "end": v(-137.1, 2.15) * mm});
            skEllipticalArc(sketch, "E67.3.0.4", {});
            skEllipticalArc(sketch, "E67.3.0.5", {});
            skLineSegment(sketch, "E67.3.0.6", {"start": v(-136.64, 2.1) * mm, "end": v(-119.14, 2.1) * mm});
            skEllipticalArc(sketch, "E67.3.0.7", {});
            skLineSegment(sketch, "E67.4.0.0", {"start": v(-133.15, 15.69) * mm, "end": v(-150.66, 15.69) * mm});
            skEllipticalArc(sketch, "E67.4.0.1", {});
            skLineSegment(sketch, "E67.4.0.2", {"start": v(-83.68, 3.04) * mm, "end": v(-132.7, 15.63) * mm});
            skLineSegment(sketch, "E67.4.0.3", {"start": v(-151.12, 14.74) * mm, "end": v(-102.1, 2.15) * mm});
            skEllipticalArc(sketch, "E67.4.0.4", {});
            skEllipticalArc(sketch, "E67.4.0.5", {});
            skLineSegment(sketch, "E67.4.0.6", {"start": v(-101.64, 2.1) * mm, "end": v(-84.14, 2.1) * mm});
            skEllipticalArc(sketch, "E67.4.0.7", {});
            skLineSegment(sketch, "E67.5.0.0", {"start": v(-98.15, 15.69) * mm, "end": v(-115.66, 15.69) * mm});
            skEllipticalArc(sketch, "E67.5.0.1", {});
            skLineSegment(sketch, "E67.5.0.2", {"start": v(-48.68, 3.04) * mm, "end": v(-97.7, 15.63) * mm});
            skLineSegment(sketch, "E67.5.0.3", {"start": v(-116.12, 14.74) * mm, "end": v(-67.1, 2.15) * mm});
            skEllipticalArc(sketch, "E67.5.0.4", {});
            skEllipticalArc(sketch, "E67.5.0.5", {});
            skLineSegment(sketch, "E67.5.0.6", {"start": v(-66.64, 2.1) * mm, "end": v(-49.14, 2.1) * mm});
            skEllipticalArc(sketch, "E67.5.0.7", {});
            skLineSegment(sketch, "E67.6.0.0", {"start": v(-63.15, 15.69) * mm, "end": v(-80.66, 15.69) * mm});
            skEllipticalArc(sketch, "E67.6.0.1", {});
            skLineSegment(sketch, "E67.6.0.2", {"start": v(-13.68, 3.04) * mm, "end": v(-62.7, 15.63) * mm});
            skLineSegment(sketch, "E67.6.0.3", {"start": v(-81.12, 14.74) * mm, "end": v(-32.1, 2.15) * mm});
            skEllipticalArc(sketch, "E67.6.0.4", {});
            skEllipticalArc(sketch, "E67.6.0.5", {});
            skLineSegment(sketch, "E67.6.0.6", {"start": v(-31.64, 2.1) * mm, "end": v(-14.14, 2.1) * mm});
            skEllipticalArc(sketch, "E67.6.0.7", {});
            skLineSegment(sketch, "E67.direction1", {"start": v(-290.66, 15.69) * mm, "end": v(-255.66, 15.69) * mm, "construction": true});
            const initialGuessF10  = {"E66.0.1": [-0.2906611710527277, 0.015186533479473206, -1, 0, 0.001, 0.0005, 4.71238898038469, 1.09624034451628], "E66.0.3": [-0.24164270818244363, 0.0025958767962970947, -1, 0, 0.001, 0.0005, 1.0962403445163043, 1.5707963267948966], "E66.0.5": [-0.22413507475945824, 0.0025958767962970947, -1, 0, 0.001, 0.0005, 1.5707963267948966, 4.237832998106066], "E66.0.7": [-0.27315353762974237, 0.01518653347947322, -1, 0, 0.001, 0.0005, 4.237832998106135, 4.71238898038469], "E67.1.0.1": [-0.2381535376297424, 0.01518653347947322, -1, 0, 0.001, 0.0005, 4.237832998106135, 4.71238898038469], "E67.1.0.4": [-0.25566117105272773, 0.015186533479473206, -1, 0, 0.001, 0.0005, 4.71238898038469, 1.0962403445162805], "E67.1.0.5": [-0.20664270818244365, 0.0025958767962970947, -1, 0, 0.001, 0.0005, 1.0962403445163043, 1.5707963267948966], "E67.1.0.7": [-0.18913507475945826, 0.0025958767962970947, -1, 0, 0.001, 0.0005, 1.5707963267948966, 4.237832998106066], "E67.2.0.1": [-0.20315353762974242, 0.01518653347947322, -1, 0, 0.001, 0.0005, 4.237832998106135, 4.71238898038469], "E67.2.0.4": [-0.22066117105272776, 0.015186533479473206, -1, 0, 0.001, 0.0005, 4.71238898038469, 1.0962403445162805], "E67.2.0.5": [-0.17164270818244368, 0.0025958767962970947, -1, 0, 0.001, 0.0005, 1.0962403445163043, 1.5707963267948966], "E67.2.0.7": [-0.15413507475945828, 0.0025958767962970947, -1, 0, 0.001, 0.0005, 1.5707963267948966, 4.237832998106066], "E67.3.0.1": [-0.16815353762974244, 0.01518653347947322, -1, 0, 0.001, 0.0005, 4.237832998106135, 4.71238898038469], "E67.3.0.4": [-0.18566117105272778, 0.015186533479473206, -1, 0, 0.001, 0.0005, 4.71238898038469, 1.0962403445162805], "E67.3.0.5": [-0.1366427081824437, 0.0025958767962970947, -1, 0, 0.001, 0.0005, 1.0962403445163043, 1.5707963267948966], "E67.3.0.7": [-0.11913507475945831, 0.0025958767962970947, -1, 0, 0.001, 0.0005, 1.5707963267948966, 4.237832998106066], "E67.4.0.1": [-0.13315353762974247, 0.01518653347947322, -1, 0, 0.001, 0.0005, 4.237832998106135, 4.71238898038469], "E67.4.0.4": [-0.1506611710527278, 0.015186533479473206, -1, 0, 0.001, 0.0005, 4.71238898038469, 1.0962403445162805], "E67.4.0.5": [-0.10164270818244373, 0.0025958767962970947, -1, 0, 0.001, 0.0005, 1.0962403445163043, 1.5707963267948966], "E67.4.0.7": [-0.08413507475945833, 0.0025958767962970947, -1, 0, 0.001, 0.0005, 1.5707963267948966, 4.237832998106066], "E67.5.0.1": [-0.0981535376297425, 0.01518653347947322, -1, 0, 0.001, 0.0005, 4.237832998106135, 4.71238898038469], "E67.5.0.4": [-0.11566117105272783, 0.015186533479473206, -1, 0, 0.001, 0.0005, 4.71238898038469, 1.0962403445162805], "E67.5.0.5": [-0.06664270818244375, 0.0025958767962970947, -1, 0, 0.001, 0.0005, 1.0962403445163043, 1.5707963267948966], "E67.5.0.7": [-0.04913507475945836, 0.0025958767962970947, -1, 0, 0.001, 0.0005, 1.5707963267948966, 4.237832998106066], "E67.6.0.1": [-0.06315353762974252, 0.01518653347947322, -1, 0, 0.001, 0.0005, 4.237832998106135, 4.71238898038469], "E67.6.0.4": [-0.08066117105272785, 0.015186533479473206, -1, 0, 0.001, 0.0005, 4.71238898038469, 1.0962403445162805], "E67.6.0.5": [-0.031642708182443774, 0.0025958767962970947, -1, 0, 0.001, 0.0005, 1.0962403445163043, 1.5707963267948966], "E67.6.0.7": [-0.014135074759458383, 0.0025958767962970947, -1, 0, 0.001, 0.0005, 1.5707963267948966, 4.237832998106066]};
            skSetInitialGuess(sketch, initialGuessF10);
            skSolve(sketch);
        }
        {
            var Q0;
            Q0 = qSketchRegion(id + "F10", true);
            extrude(context, id + "F11", {"entities" : qUnion([Q0]), "operationType" : NewBodyOperationType.REMOVE, "oppositeDirection" : true, "depth" : 230 * mm, "offsetDistance" : 25 * mm, "hasSecondDirection" : true, "secondDirectionOppositeDirection" : true, "secondDirectionDepth" : 69 * mm});
        }
        {
            var Q0;
            Q0 = qSketchRegion(id + "F10", true);
            extrude(context, id + "F12", {"entities" : qUnion([Q0]), "operationType" : NewBodyOperationType.REMOVE, "depth" : 250 * mm, "offsetDistance" : 25 * mm, "hasSecondDirection" : true, "secondDirectionOppositeDirection" : false, "secondDirectionDepth" : 69 * mm});
        }
    });
